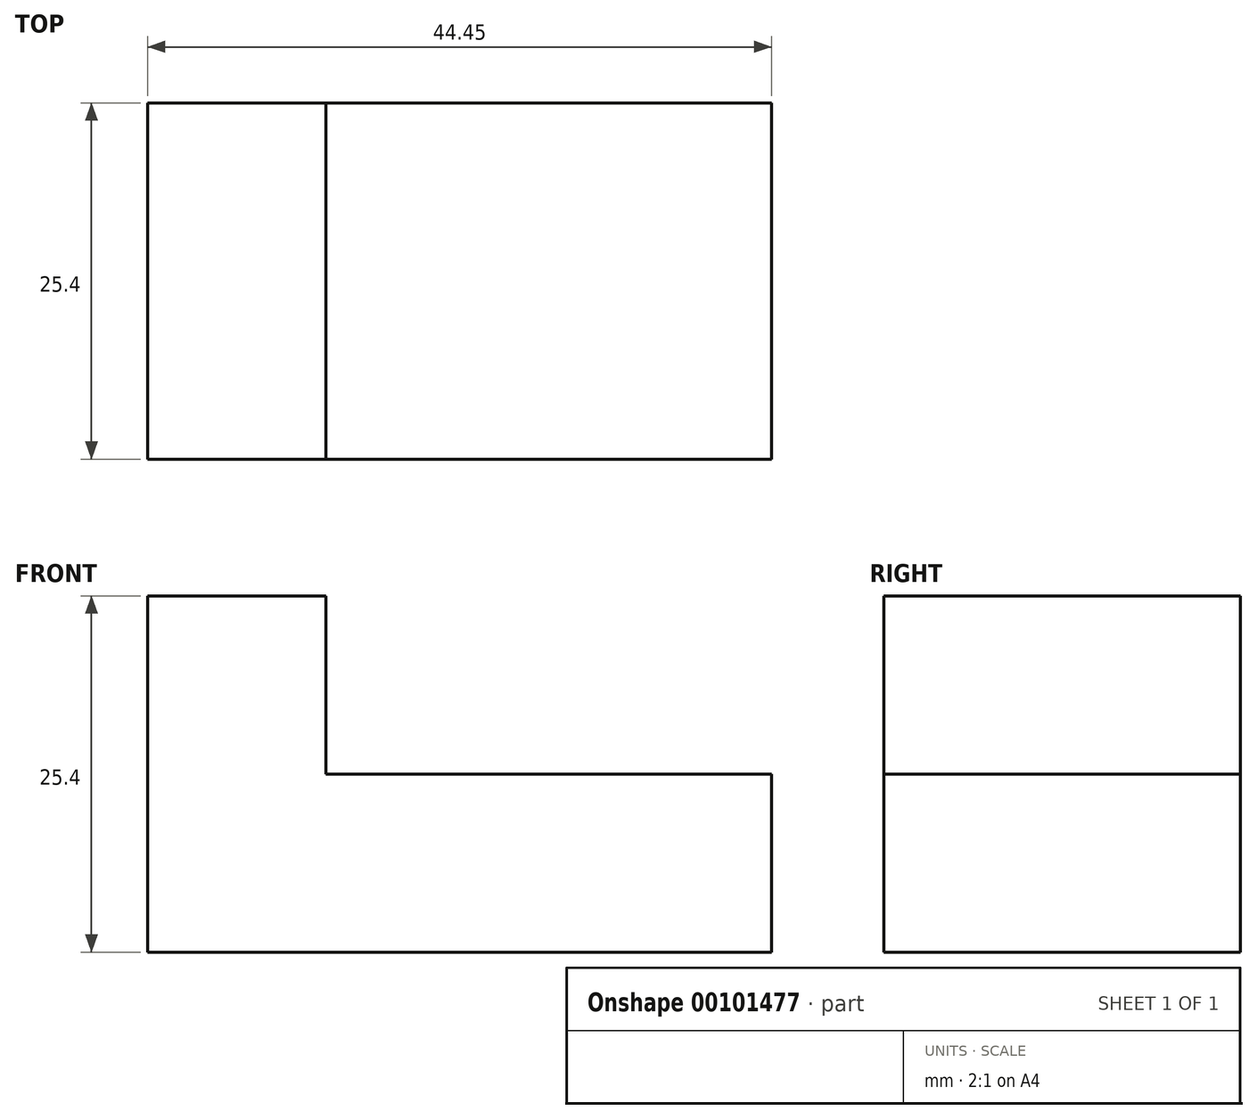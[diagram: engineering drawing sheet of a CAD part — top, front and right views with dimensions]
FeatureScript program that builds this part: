
annotation { "Feature Type Name" : "Feature", "Feature Type Description" : "" }
export const myFeature = defineFeature(function(context is Context, id is Id, definition is map)
    precondition{}
    {
        {
            var Q0;
            Q0=qCreatedBy(makeId("Front.planeOp"),FACE);
            var sketch = newSketch(context, id + "F0", { "sketchPlane" : qUnion([Q0])});
            skLineSegment(sketch, "E0", {"start": v(0, 0) * mm, "end": v(44.45, 0) * mm});
            skLineSegment(sketch, "E1", {"start": v(44.45, 0) * mm, "end": v(44.45, 12.7) * mm});
            skLineSegment(sketch, "E2", {"start": v(44.45, 12.7) * mm, "end": v(12.7, 12.7) * mm});
            skLineSegment(sketch, "E3", {"start": v(12.7, 12.7) * mm, "end": v(12.7, 25.4) * mm});
            skLineSegment(sketch, "E4", {"start": v(12.7, 25.4) * mm, "end": v(0, 25.4) * mm});
            skLineSegment(sketch, "E5", {"start": v(0, 25.4) * mm, "end": v(0, 0) * mm});
            skSolve(sketch);
        }
        {
            var Q0;
            Q0=makeQuery(id+"F0.imprint","IMPRINT",FACE,{"disambiguationData":[TD([[makeQuery(id+"F0.imprint","IMPRINT",EDGE,{"derivedFrom":sQuery(id+"F0.wireOp",EDGE,"E0")}),1.0]])]});
            extrude(context, id + "F1", {"entities" : qUnion([Q0]), "depth" : 25.4 * mm});
        }
    });
